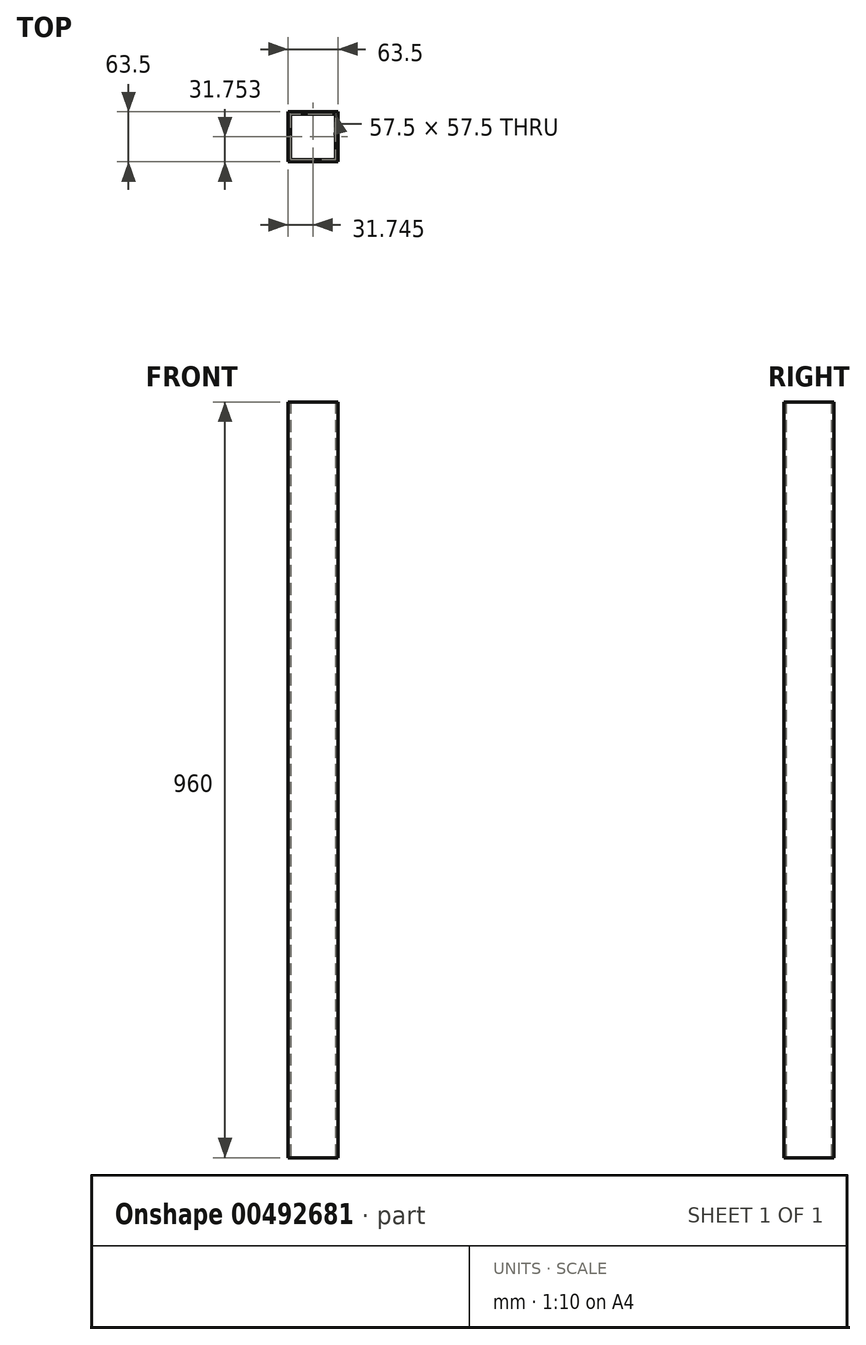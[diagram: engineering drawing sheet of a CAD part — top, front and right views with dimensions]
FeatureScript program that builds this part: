
annotation { "Feature Type Name" : "Feature", "Feature Type Description" : "" }
export const myFeature = defineFeature(function(context is Context, id is Id, definition is map)
    precondition{}
    {
        {
            var Q0;
            Q0=qCreatedBy(makeId("Top.planeOp"),FACE);
            var sketch = newSketch(context, id + "F0", { "sketchPlane" : qUnion([Q0])});
            skLineSegment(sketch, "E0.bottom", {"start": v(-36.01, 35.07) * mm, "end": v(27.49, 35.07) * mm});
            skLineSegment(sketch, "E0.top", {"start": v(-36.01, -28.43) * mm, "end": v(27.49, -28.43) * mm});
            skLineSegment(sketch, "E0.left", {"start": v(-36.01, 35.07) * mm, "end": v(-36.01, -28.43) * mm});
            skLineSegment(sketch, "E0.right", {"start": v(27.49, 35.07) * mm, "end": v(27.49, -28.43) * mm});
            skLineSegment(sketch, "E1.bottom", {"start": v(-33.01, 32.07) * mm, "end": v(24.49, 32.07) * mm});
            skLineSegment(sketch, "E1.top", {"start": v(-33.01, -25.43) * mm, "end": v(24.49, -25.43) * mm});
            skLineSegment(sketch, "E1.left", {"start": v(-33.01, 32.07) * mm, "end": v(-33.01, -25.43) * mm});
            skLineSegment(sketch, "E1.right", {"start": v(24.49, 32.07) * mm, "end": v(24.49, -25.43) * mm});
            skSolve(sketch);
        }
        {
            var Q0;
            Q0 = qSketchRegion(id + "F0", true);
            extrude(context, id + "F1", {"entities" : qUnion([Q0]), "depth" : 960 * mm});
        }
    });
